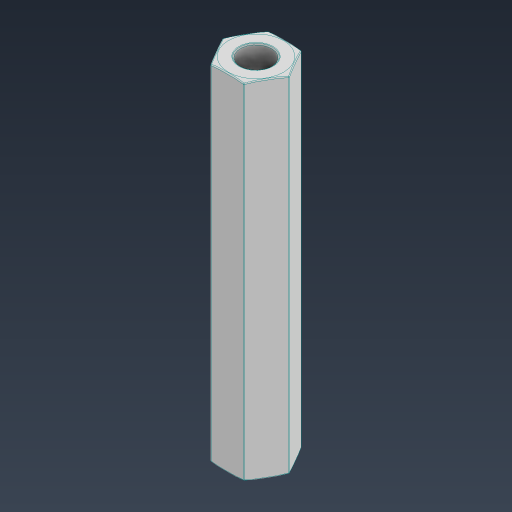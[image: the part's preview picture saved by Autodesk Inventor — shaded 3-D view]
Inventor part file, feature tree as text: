
AUTODESK INVENTOR PART (.ipt)
format: ipt  version: 2024.3 (Build 283343000, 343)  size: 185,344 bytes
history: native  units: in
note: dims shown in document units (in); Inventor stores cm internally (conversion verified against a paired STEP export)
features: fillet x1
ambient origin geometry x8: Origin, YZ Plane, XZ Plane, XY Plane, X Axis, Y Axis, Z Axis, Center Point
bodies: Solid1 (feature_tree)
feature tree (1):
  fillet  "Fillet1"  [1 undecoded]
note: 1 required parameter value undecoded (feature->parameter linkage not recoverable at this tier; creation-order binding heuristic only, values carry confidence <= 0.55)
